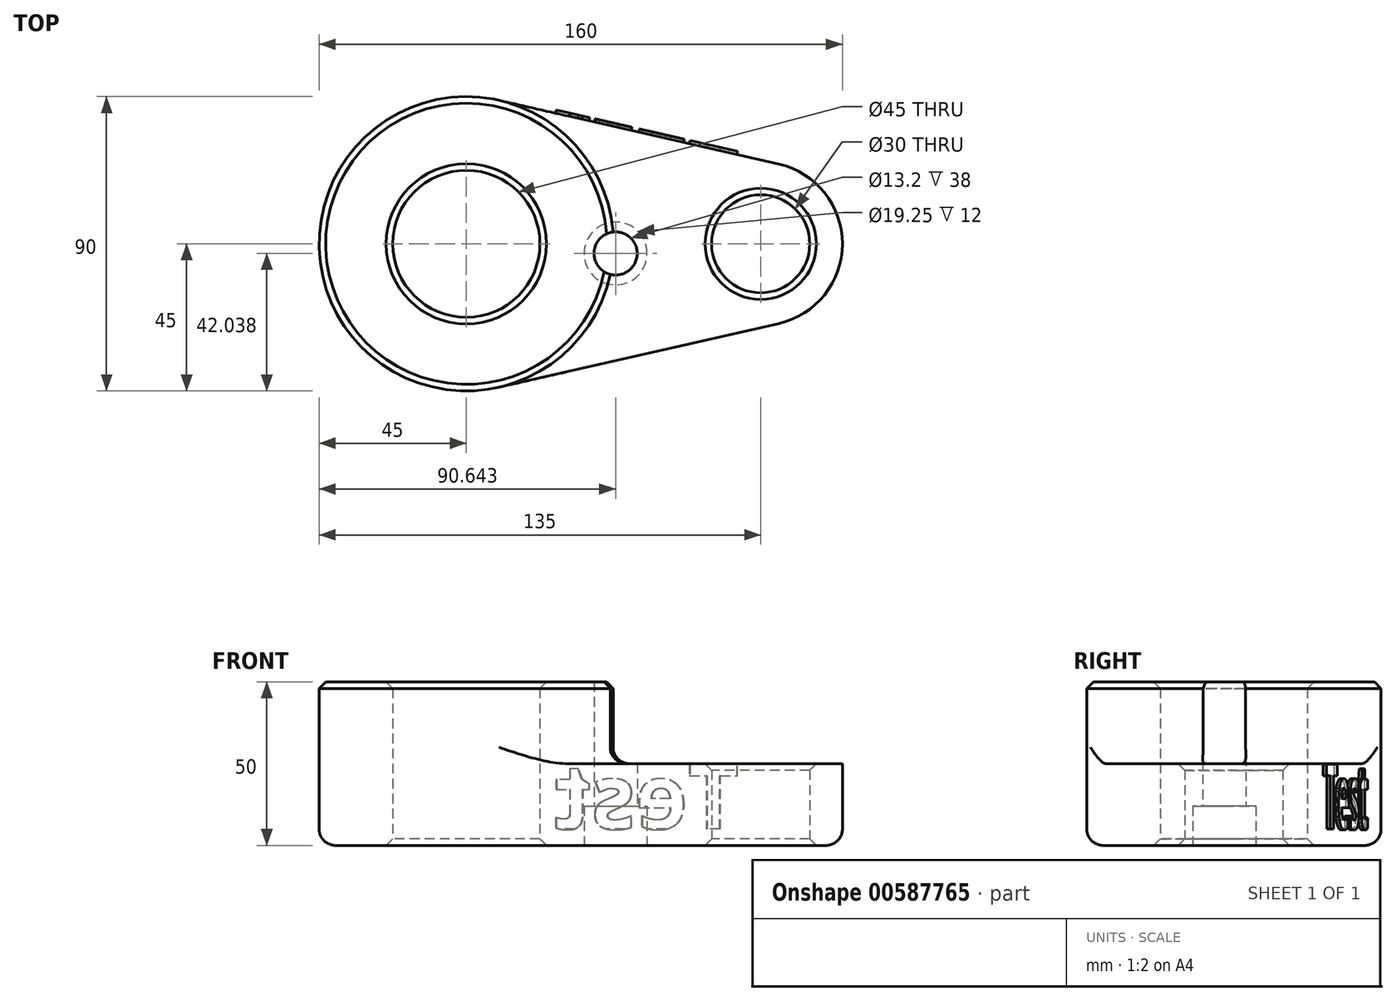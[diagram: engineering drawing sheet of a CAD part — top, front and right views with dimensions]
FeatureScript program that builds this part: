
annotation { "Feature Type Name" : "Feature", "Feature Type Description" : "" }
export const myFeature = defineFeature(function(context is Context, id is Id, definition is map)
    precondition{}
    {
        {
            var Q0;
            Q0=qCreatedBy(makeId("Top.planeOp"),FACE);
            var sketch = newSketch(context, id + "F0", { "sketchPlane" : qUnion([Q0])});
            skCircle(sketch, "E0", {"center": v(0, 0) * mm, "radius": 45 * mm});
            skCircle(sketch, "E1", {"center": v(90, 0) * mm, "radius": 25 * mm});
            skLineSegment(sketch, "E2", {"start": v(95.56, 24.37) * mm, "end": v(10, 43.87) * mm});
            skLineSegment(sketch, "E3", {"start": v(10, -43.87) * mm, "end": v(95.56, -24.37) * mm});
            skCircle(sketch, "E4", {"center": v(0, 0) * mm, "radius": 22.5 * mm});
            skCircle(sketch, "E5", {"center": v(90, 0) * mm, "radius": 15 * mm});
            skSolve(sketch);
        }
        {
            var Q0;
            Q0 = qSketchRegion(id + "F0", true);
            extrude(context, id + "F1", {"entities" : qUnion([Q0]), "depth" : 25 * mm, "offsetDistance" : 25 * mm});
        }
        {
            var Q0;
            Q0=makeQuery(id+"F0.imprint","IMPRINT",FACE,{"disambiguationData":[TD([[makeQuery(id+"F0.imprint","IMPRINT",EDGE,{"derivedFrom":sQuery(id+"F0.wireOp",EDGE,"E4")}),-1.0]])]});
            extrude(context, id + "F2", {"entities" : qUnion([Q0]), "operationType" : NewBodyOperationType.ADD, "depth" : 50 * mm, "offsetDistance" : 25 * mm});
        }
        {
            var Q0;
            Q0=makeQuery(id+"F2.opExtrude","CAP_EDGE",EDGE,{"disambiguationData":[OSD([sQuery(id+"F0.wireOp",EDGE,"E0")])],"isStart":false});
            var Q1;
            Q1=makeQuery(id+"F2.opExtrude","CAP_EDGE",EDGE,{"disambiguationData":[OSD([sQuery(id+"F0.wireOp",EDGE,"E4")])],"isStart":false});
            var Q2;
            Q2=makeQuery(id+"F1.opExtrude","CAP_EDGE",EDGE,{"disambiguationData":[OSD([sQuery(id+"F0.wireOp",EDGE,"E5")])],"isStart":false});
            chamfer(context, id + "F3", {"entities" : qUnion([Q0, Q1, Q2]), "width" : 2 * mm, "tangentPropagation" : true});
        }
        {
            var Q0;
            {var subQ0=sQuery(id+"F0.wireOp",EDGE,"E0");Q0=makeQuery(id+"F2.boolean.opBoolean","INTERSECT",EDGE,{"derivedFrom":[makeQuery(id+"F1.opExtrude","CAP_FACE",FACE,{"disambiguationData":[OSD([subQ0,sQuery(id+"F0.wireOp",EDGE,"E2"),sQuery(id+"F0.wireOp",EDGE,"E3"),sQuery(id+"F0.wireOp",EDGE,"E4"),sQuery(id+"F0.wireOp",EDGE,"E1"),sQuery(id+"F0.wireOp",EDGE,"E5")])],"isStart":false}),makeQuery(id+"F2.opExtrude","SWEPT_FACE",FACE,{"disambiguationData":[OSD([subQ0])]})]});}
            fillet(context, id + "F4", {"entities" : qUnion([Q0]), "radius" : 5 * mm, "tangentPropagation" : true, "allowEdgeOverflow" : false});
        }
        {
            var Q0;
            Q0=makeQuery(id+"F1.opExtrude","CAP_EDGE",EDGE,{"disambiguationData":[OSD([sQuery(id+"F0.wireOp",EDGE,"E3")])],"isStart":true});
            fillet(context, id + "F5", {"entities" : qUnion([Q0]), "radius" : 5 * mm, "tangentPropagation" : true, "allowEdgeOverflow" : false});
        }
        {
            var Q0;
            Q0=makeQuery(id+"F1.opExtrude","CAP_EDGE",EDGE,{"disambiguationData":[OSD([sQuery(id+"F0.wireOp",EDGE,"E4")])],"isStart":true});
            var Q1;
            Q1=makeQuery(id+"F1.opExtrude","CAP_EDGE",EDGE,{"disambiguationData":[OSD([sQuery(id+"F0.wireOp",EDGE,"E5")])],"isStart":true});
            chamfer(context, id + "F6", {"entities" : qUnion([Q0, Q1]), "width" : 2 * mm, "tangentPropagation" : true});
        }
        {
            var Q0;
            Q0=makeQuery(id+"F1.opExtrude","CAP_FACE",FACE,{"disambiguationData":[OSD([sQuery(id+"F0.wireOp",EDGE,"E0"),sQuery(id+"F0.wireOp",EDGE,"E2"),sQuery(id+"F0.wireOp",EDGE,"E3"),sQuery(id+"F0.wireOp",EDGE,"E4"),sQuery(id+"F0.wireOp",EDGE,"E1"),sQuery(id+"F0.wireOp",EDGE,"E5")])],"isStart":true});
            var sketch = newSketch(context, id + "F7", { "sketchPlane" : qUnion([Q0])});
            skPoint(sketch, "E6", {"position": v(45.64, 2.96) * mm});
            skSolve(sketch);
        }
        {
            var Q0;
            Q0=sQuery(id+"F7.wireOp",VERTEX,"E6");
            var Q1;
            Q1=makeQuery(id+"F1.opExtrude","SWEPT_BODY",BODY,{"disambiguationData":[OSD([sQuery(id+"F0.wireOp",EDGE,"E0"),sQuery(id+"F0.wireOp",EDGE,"E2"),sQuery(id+"F0.wireOp",EDGE,"E3"),sQuery(id+"F0.wireOp",EDGE,"E4"),sQuery(id+"F0.wireOp",EDGE,"E1"),sQuery(id+"F0.wireOp",EDGE,"E5")])]});
            hole(context, id + "F8", {"style" : HoleStyle.C_BORE, "endStyle" : HoleEndStyle.THROUGH, "standardTappedOrClearance" : lookupTablePath({ "standard" : "ISO", "fit" : "Normal", "size" : "M12", "type" : "Clearance" }), "standardBlindInLast" : lookupTablePath({ "fit" : "Standard", "standard" : "ISO", "size" : "M12", "type" : "Clearance" }), "holeDiameter" : 13.2 * mm, "cBoreDiameter" : 19.25 * mm, "cBoreDepth" : 12 * mm, "majorDiameter" : 5 * mm, "isTappedThrough" : true, "tappedDepth" : 12 * mm, "tapClearance" : 3, "locations" : qUnion([Q0]), "scope" : qUnion([Q1])});
        }
        {
            var Q0;
            Q0=makeQuery(id+"F1.opExtrude","SWEPT_FACE",FACE,{"disambiguationData":[OSD([sQuery(id+"F0.wireOp",EDGE,"E2")])]});
            var sketch = newSketch(context, id + "F9", { "sketchPlane" : qUnion([Q0])});
            skText(sketch, "E7", { "text": "Test", "fontName": "OpenSans-Bold.ttf"});
            const initialGuessF9  = {"E7": [-0.07515, 0.005, 1, 0, 0.02]};
            skSetInitialGuess(sketch, initialGuessF9);
            skSolve(sketch);
        }
        {
            var Q0;
            Q0 = qSketchRegion(id + "F9", true);
            extrude(context, id + "F10", {"entities" : qUnion([Q0]), "operationType" : NewBodyOperationType.ADD, "depth" : 1 * mm, "offsetDistance" : 25 * mm});
        }
    });
